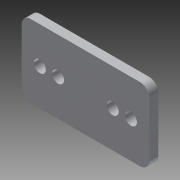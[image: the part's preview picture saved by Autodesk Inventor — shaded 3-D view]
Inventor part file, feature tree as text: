
AUTODESK INVENTOR PART (.ipt)
format: ipt  version: 2014 (Build 180170000, 170)  size: 96,768 bytes
history: native  units: in
note: dims shown in document units (in); Inventor stores cm internally (conversion verified against a paired STEP export)
features: extrude x1, sketch x1
ambient origin geometry x8: Origin, YZ Plane, XZ Plane, XY Plane, X Axis, Y Axis, Z Axis, Center Point
bodies: Solid1 (feature_tree)
feature tree (2):
  extrude  "Extrusion1"  Depth=1.0in
  sketch  "Sketch1"  dims[d0=1.75in d1=1.0in d2=0.163in d3=0.25in d5=0.7874in d7=1.0in d8=0.3937in d10=1.0in d12=0.25in d13=0.7874in d15=1.0in d16=0.3937in d18=1.0in d20=0.125in d21=0.125in d22=0.0in]
